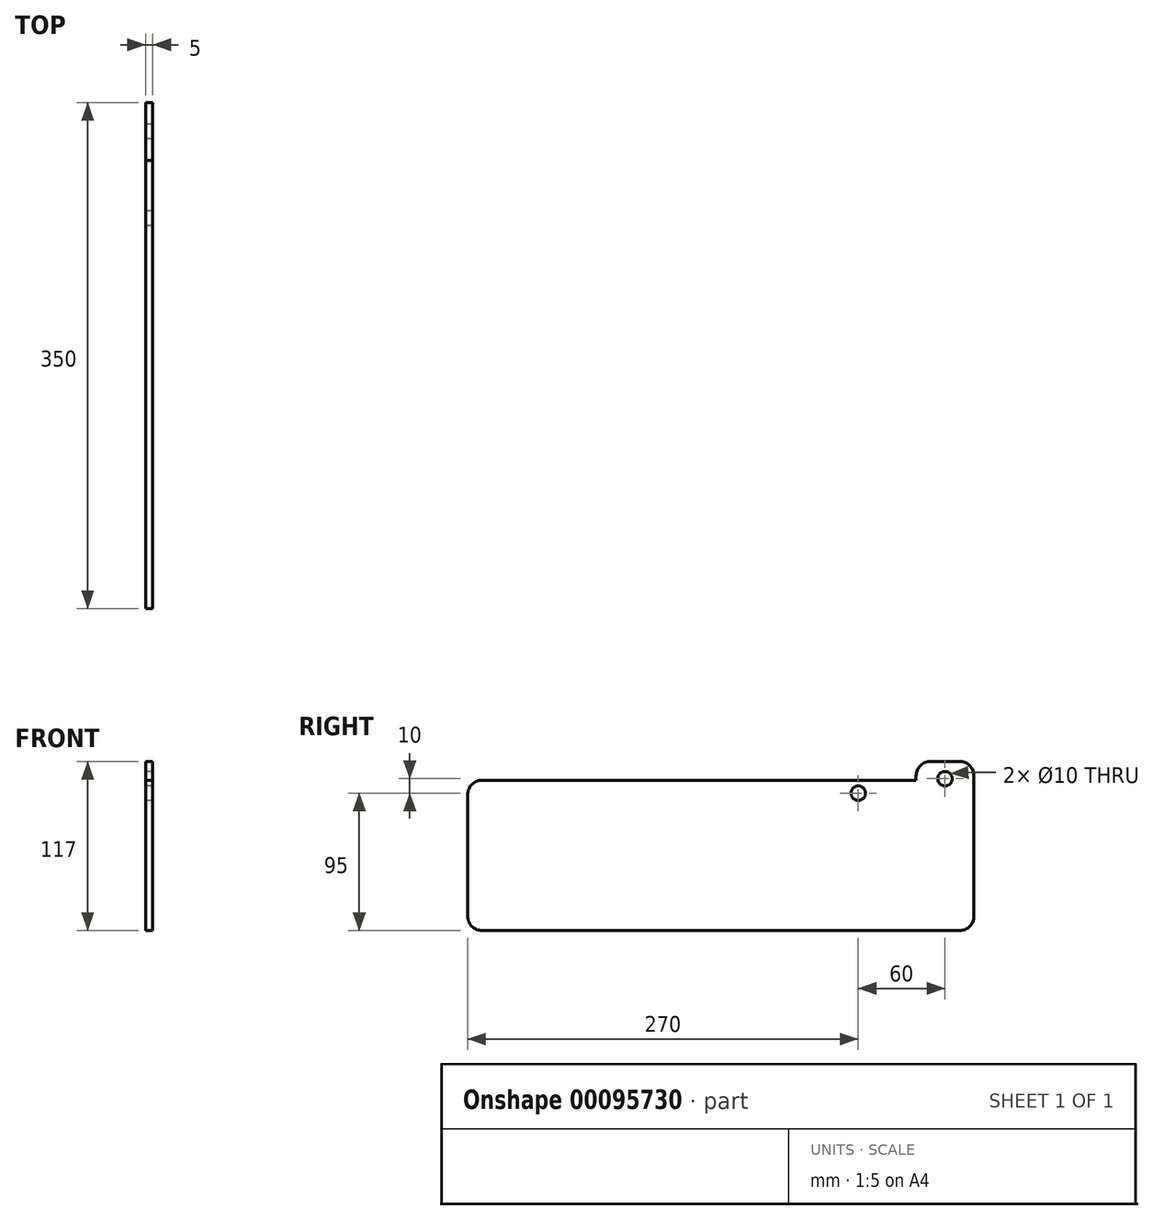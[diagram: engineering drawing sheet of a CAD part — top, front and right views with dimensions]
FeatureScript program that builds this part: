
annotation { "Feature Type Name" : "Feature", "Feature Type Description" : "" }
export const myFeature = defineFeature(function(context is Context, id is Id, definition is map)
    precondition{}
    {
        {
            var Q0;
            Q0=qCreatedBy(makeId("Right.planeOp"),FACE);
            var sketch = newSketch(context, id + "F0", { "sketchPlane" : qUnion([Q0])});
            skLineSegment(sketch, "E0", {"start": v(-320, -1) * mm, "end": v(-20, -1) * mm});
            skLineSegment(sketch, "E1", {"start": v(-20, -1) * mm, "end": v(-20, 2) * mm});
            skLineSegment(sketch, "E2", {"start": v(-10, 12) * mm, "end": v(10, 12) * mm});
            skLineSegment(sketch, "E3", {"start": v(20, 2) * mm, "end": v(20, -95) * mm});
            skLineSegment(sketch, "E4", {"start": v(10, -105) * mm, "end": v(-320, -105) * mm});
            skLineSegment(sketch, "E5", {"start": v(-330, -95) * mm, "end": v(-330, -11) * mm});
            skCircle(sketch, "E6", {"center": v(0, 0) * mm, "radius": 5 * mm});
            skCircle(sketch, "E7", {"center": v(-60, -10) * mm, "radius": 5 * mm});
            skPoint(sketch, "E8.visualSharp", {"position": v(20, -105) * mm});
            skArc(sketch, "E8.filletArc", {"start": v(10, -105) * mm, "mid": v(17.07, -102.07) * mm, "end": v(20, -95) * mm});
            skPoint(sketch, "E9.visualSharp", {"position": v(-330, -105) * mm});
            skArc(sketch, "E9.filletArc", {"start": v(-330, -95) * mm, "mid": v(-327.07, -102.07) * mm, "end": v(-320, -105) * mm});
            skPoint(sketch, "E10.visualSharp", {"position": v(-330, -1) * mm});
            skArc(sketch, "E10.filletArc", {"start": v(-320, -1) * mm, "mid": v(-327.07, -3.93) * mm, "end": v(-330, -11) * mm});
            skPoint(sketch, "E11.visualSharp", {"position": v(-20, 12) * mm});
            skArc(sketch, "E11.filletArc", {"start": v(-10, 12) * mm, "mid": v(-17.07, 9.07) * mm, "end": v(-20, 2) * mm});
            skPoint(sketch, "E12.visualSharp", {"position": v(20, 12) * mm});
            skArc(sketch, "E12.filletArc", {"start": v(20, 2) * mm, "mid": v(17.07, 9.07) * mm, "end": v(10, 12) * mm});
            skSolve(sketch);
        }
        {
            var Q0;
            Q0=makeQuery(id+"F0.imprint","IMPRINT",FACE,{"disambiguationData":[TD([[makeQuery(id+"F0.imprint","IMPRINT",EDGE,{"derivedFrom":sQuery(id+"F0.wireOp",EDGE,"E0")}),-1.0]])]});
            var Q1;
            Q1=qSketchRegion(id+"F0",true);
            extrude(context, id + "F1", {"entities" : qUnion([Q0, Q1]), "depth" : 5 * mm});
        }
    });
